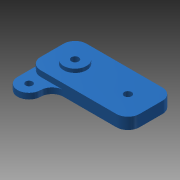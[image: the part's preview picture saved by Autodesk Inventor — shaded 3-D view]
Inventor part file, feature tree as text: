
AUTODESK INVENTOR PART (.ipt)
format: ipt  version: 2013 (Build 170138000, 138)  size: 124,928 bytes
history: native  units: mm
features: extrude x3, sketch x3, fillet x2
ambient origin geometry x8: Origin, YZ Plane, XZ Plane, XY Plane, X Axis, Y Axis, Z Axis, Center Point
bodies: Solid1 (feature_tree)
feature tree (8):
  extrude  "Extrusion1"  Depth=3.2mm
  extrude  "Extrusion2"  Depth=10.0mm
  fillet  "Fillet2"  Radius=10.0mm
  extrude  "Extrusion3"  Depth=23.0mm
  fillet  "Fillet3"  Radius=10.0mm
  sketch  "Sketch1"  dims[d2=20.0mm d3=3.2mm]
  sketch  "Sketch2"  dims[d4=3.2mm d5=10.0mm d6=10.0mm]
  sketch  "Sketch3"  dims[d7=5.0mm d8=0.0mm d10=23.0mm d11=10.0mm d12=1.6mm d13=0.0mm d15=10.0mm d16=10.0mm d17=3.0mm d18=5.0mm d19=2.5mm d20=0.0mm d21=5.0mm]
